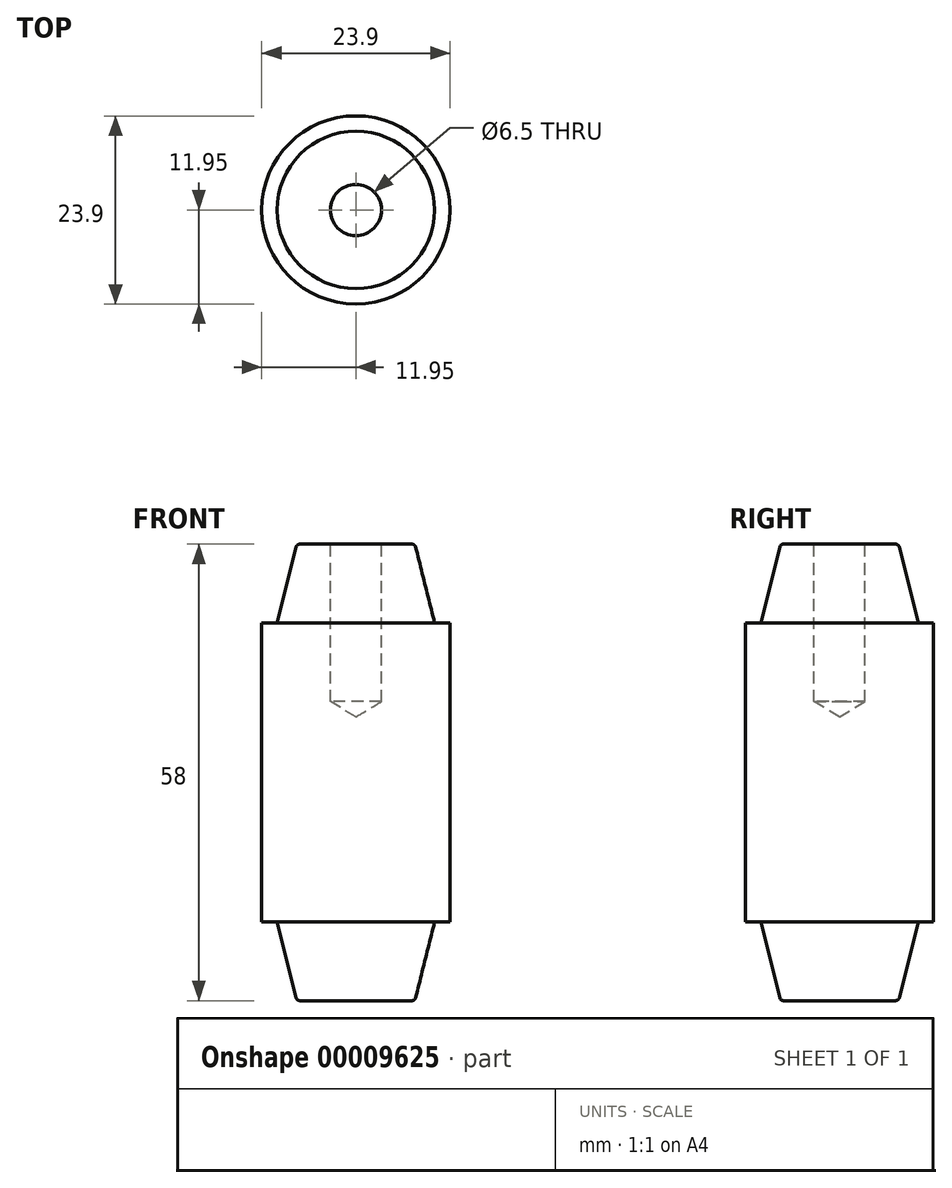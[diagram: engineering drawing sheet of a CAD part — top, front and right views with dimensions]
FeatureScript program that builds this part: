
annotation { "Feature Type Name" : "Feature", "Feature Type Description" : "" }
export const myFeature = defineFeature(function(context is Context, id is Id, definition is map)
    precondition{}
    {
        {
            var Q0;
            Q0=qCreatedBy(makeId("Front.planeOp"),FACE);
            var sketch = newSketch(context, id + "F0", { "sketchPlane" : qUnion([Q0])});
            skLineSegment(sketch, "E0.rect.bottom", {"start": v(7.5, 29) * mm, "end": v(-7.5, 29) * mm});
            skLineSegment(sketch, "E0.rect.top", {"start": v(7.5, -29) * mm, "end": v(-7.5, -29) * mm});
            skLineSegment(sketch, "E0.rect.left", {"start": v(11.95, 19) * mm, "end": v(11.95, -19) * mm});
            skLineSegment(sketch, "E0.rect.right", {"start": v(-11.95, 19) * mm, "end": v(-11.95, -19) * mm});
            skPoint(sketch, "E0.rect.middle", {"position": v(0, 0) * mm});
            skLineSegment(sketch, "E1.rect.bottom", {"start": v(11.95, 19) * mm, "end": v(-11.95, 19) * mm});
            skLineSegment(sketch, "E1.rect.top", {"start": v(11.95, -19) * mm, "end": v(-11.95, -19) * mm});
            skPoint(sketch, "E2.rect.middle", {"position": v(0, 29) * mm});
            skPoint(sketch, "E3.rect.middle", {"position": v(0, 19) * mm});
            skLineSegment(sketch, "E4", {"start": v(-7.5, 29) * mm, "end": v(-10, 19) * mm});
            skLineSegment(sketch, "E5", {"start": v(7.5, 29) * mm, "end": v(10, 19) * mm});
            skPoint(sketch, "E6.rect.middle", {"position": v(0, -29) * mm});
            skPoint(sketch, "E7.rect.middle", {"position": v(0, -19) * mm});
            skLineSegment(sketch, "E8", {"start": v(-10, -19) * mm, "end": v(-7.5, -29) * mm});
            skLineSegment(sketch, "E9", {"start": v(10, -19) * mm, "end": v(7.5, -29) * mm});
            skLineSegment(sketch, "E10", {"start": v(0, 38.95) * mm, "end": v(0, -37.28) * mm});
            skSolve(sketch);
        }
        {
            var Q0;
            {var subQ5=sQuery(id+"F0.wireOp",EDGE,"E4");Q0=makeQuery(id+"F0.imprint","IMPRINT",FACE,{"disambiguationData":[TD([[makeQuery(id+"F0.imprint","IMPRINT",EDGE,{"derivedFrom":subQ5}),1.0]])]});}
            var Q1;
            {var subQ5=sQuery(id+"F0.wireOp",EDGE,"E0.rect.right");Q1=makeQuery(id+"F0.imprint","IMPRINT",FACE,{"disambiguationData":[TD([[makeQuery(id+"F0.imprint","IMPRINT",EDGE,{"derivedFrom":subQ5}),1.0]])]});}
            var Q2;
            {var subQ5=sQuery(id+"F0.wireOp",EDGE,"E8");Q2=makeQuery(id+"F0.imprint","IMPRINT",FACE,{"disambiguationData":[TD([[makeQuery(id+"F0.imprint","IMPRINT",EDGE,{"derivedFrom":subQ5}),1.0]])]});}
            var Q3;
            Q3=sQuery(id+"F0.wireOp",EDGE,"E10");
            revolve(context, id + "F1", {"entities" : qUnion([Q0, Q1, Q2]), "axis" : qUnion([Q3]), "revolveType" : RevolveType.FULL});
        }
        {
            var Q0;
            Q0=makeQuery(id+"F1.opRevolve","SWEPT_FACE",FACE,{"disambiguationData":[OSD([sQuery(id+"F0.wireOp",EDGE,"E0.rect.bottom")])]});
            var sketch = newSketch(context, id + "F2", { "sketchPlane" : qUnion([Q0])});
            skPoint(sketch, "E11", {"position": v(0, 0) * mm});
            skSolve(sketch);
        }
        {
            var Q0;
            Q0=sQuery(id+"F2.wireOp",VERTEX,"E11");
            var Q1;
            Q1=makeQuery(id+"F1.opRevolve","SWEPT_BODY",BODY,{"disambiguationData":[OSD([sQuery(id+"F0.wireOp",EDGE,"E0.rect.bottom"),sQuery(id+"F0.wireOp",EDGE,"E0.rect.top"),sQuery(id+"F0.wireOp",EDGE,"E1.rect.bottom"),sQuery(id+"F0.wireOp",EDGE,"E1.rect.top"),sQuery(id+"F0.wireOp",EDGE,"E0.rect.right"),sQuery(id+"F0.wireOp",EDGE,"E4"),sQuery(id+"F0.wireOp",EDGE,"E8"),sQuery(id+"F0.wireOp",EDGE,"E10")])]});
            hole(context, id + "F3", {"style" : HoleStyle.SIMPLE, "holeDiameter" : 6.5 * mm, "endStyle" : HoleEndStyle.BLIND, "holeDepth" : 20 * mm, "locations" : qUnion([Q0]), "scope" : qUnion([Q1])});
        }
        {
            var Q0;
            Q0=makeQuery(id+"F1.opRevolve","SWEPT_EDGE",EDGE,{"disambiguationData":[OSD([sQuery(id+"F0.wireOp",EDGE,"E0.rect.bottom"),sQuery(id+"F0.wireOp",EDGE,"E4")])]});
            fillet(context, id + "F4", {"entities" : qUnion([Q0]), "radius" : .5 * mm, "tangentPropagation" : true, "allowEdgeOverflow" : false});
        }
        {
            var Q0;
            Q0=makeQuery(id+"F1.opRevolve","SWEPT_EDGE",EDGE,{"disambiguationData":[OSD([sQuery(id+"F0.wireOp",EDGE,"E0.rect.top"),sQuery(id+"F0.wireOp",EDGE,"E8")])]});
            fillet(context, id + "F5", {"entities" : qUnion([Q0]), "radius" : .5 * mm, "tangentPropagation" : true, "allowEdgeOverflow" : false});
        }
    });
